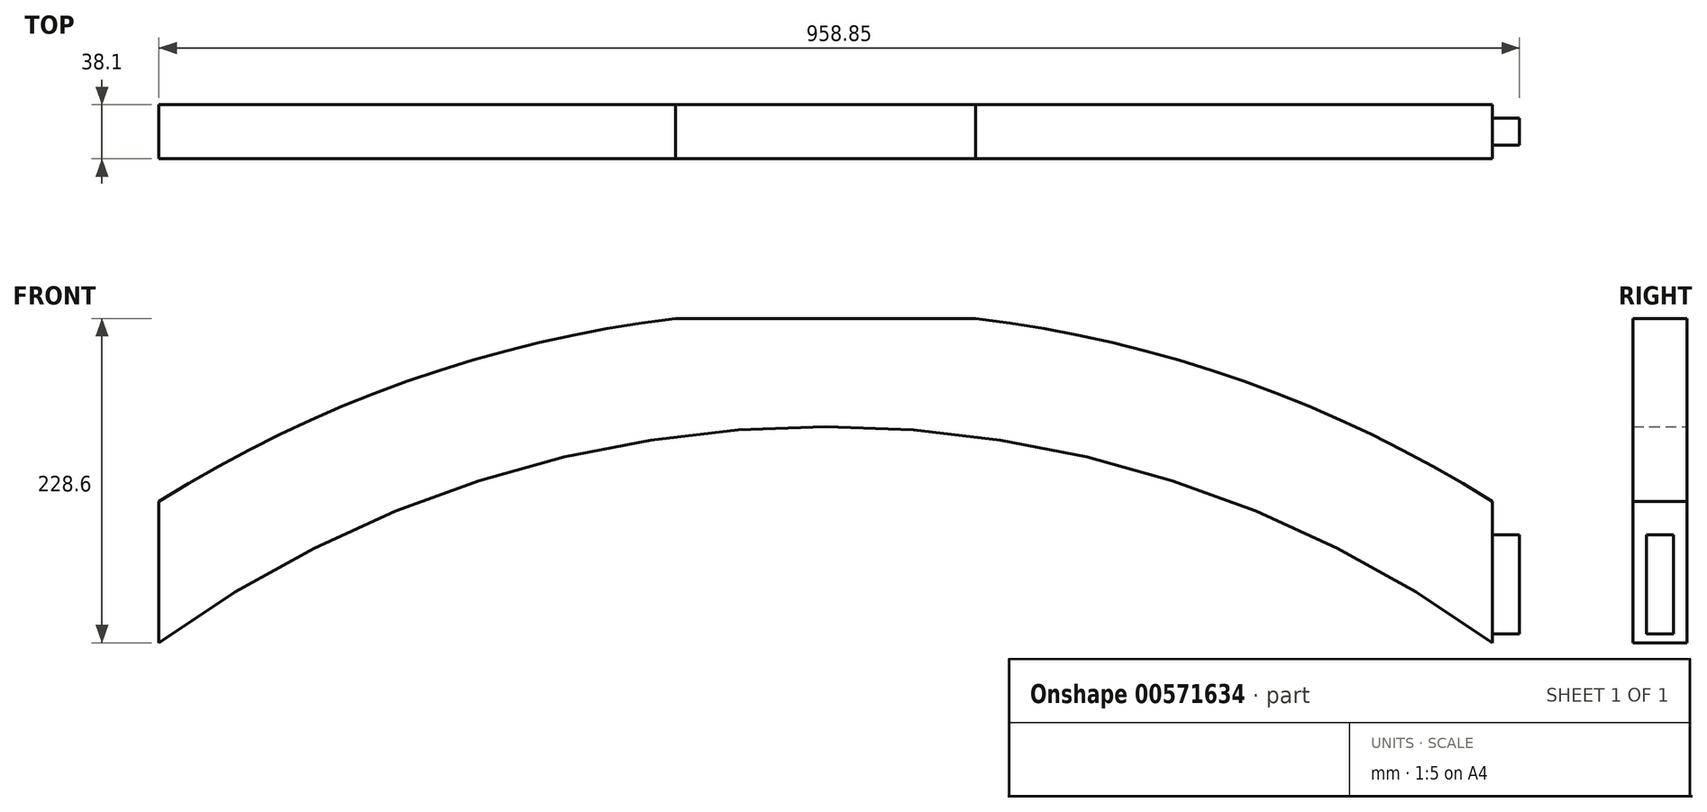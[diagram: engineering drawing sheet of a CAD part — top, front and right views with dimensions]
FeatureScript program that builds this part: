
annotation { "Feature Type Name" : "Feature", "Feature Type Description" : "" }
export const myFeature = defineFeature(function(context is Context, id is Id, definition is map)
    precondition{}
    {
        {
            var Q0;
            Q0=qCreatedBy(makeId("Front.planeOp"),FACE);
            var sketch = newSketch(context, id + "F0", { "sketchPlane" : qUnion([Q0])});
            skLineSegment(sketch, "E0.bottom", {"start": v(0, 0) * mm, "end": v(990.6, 0) * mm, "construction": true});
            skLineSegment(sketch, "E0.top", {"start": v(0, 375.92) * mm, "end": v(990.6, 375.92) * mm, "construction": true});
            skLineSegment(sketch, "E0.left", {"start": v(0, 0) * mm, "end": v(0, 375.92) * mm, "construction": true});
            skLineSegment(sketch, "E0.right", {"start": v(990.6, 0) * mm, "end": v(990.6, 375.92) * mm, "construction": true});
            skLineSegment(sketch, "E1", {"start": v(25.4, 366.92) * mm, "end": v(25.4, 21.35) * mm, "construction": true});
            skLineSegment(sketch, "E2", {"start": v(965.2, 14.82) * mm, "end": v(965.2, 359.55) * mm, "construction": true});
            skPoint(sketch, "E3", {"position": v(25.4, 147.32) * mm});
            skPoint(sketch, "E4", {"position": v(965.2, 147.32) * mm});
            skPoint(sketch, "E5", {"position": v(495.3, 299.72) * mm});
            skPoint(sketch, "E5.positionSnap0", {"position": v(495.3, 375.92) * mm});
            skArc(sketch, "E6", {"start": v(965.2, 147.32) * mm, "mid": v(495.3, 299.72) * mm, "end": v(25.4, 147.32) * mm});
            skArc(sketch, "E7.0", {"start": v(965.2, 246.89) * mm, "mid": v(790.25, 331.56) * mm, "end": v(601.02, 375.92) * mm});
            skLineSegment(sketch, "E8", {"start": v(25.4, 147.32) * mm, "end": v(25.4, 246.89) * mm});
            skLineSegment(sketch, "E9", {"start": v(965.2, 147.32) * mm, "end": v(965.2, 246.89) * mm});
            skArc(sketch, "E10.trimOffspring", {"start": v(389.58, 375.92) * mm, "mid": v(200.35, 331.56) * mm, "end": v(25.4, 246.89) * mm});
            skLineSegment(sketch, "E11", {"start": v(389.58, 375.92) * mm, "end": v(389.58, 375.92) * mm});
            skLineSegment(sketch, "E12", {"start": v(389.58, 375.92) * mm, "end": v(601.02, 375.92) * mm});
            skLineSegment(sketch, "E13.left", {"start": v(25.4, 217.17) * mm, "end": v(25.4, 153.67) * mm});
            skSolve(sketch);
        }
        {
            var Q0;
            {var subQ3=sQuery(id+"F0.wireOp",EDGE,"E6");Q0=makeQuery(id+"F0.imprint","IMPRINT",FACE,{"disambiguationData":[TD([[makeQuery(id+"F0.imprint","IMPRINT",EDGE,{"derivedFrom":subQ3}),-1.0]])]});}
            extrude(context, id + "F1", {"entities" : qUnion([Q0]), "depth" : 38.1 * mm, "offsetDistance" : 25.4 * mm});
        }
        {
            var Q0;
            Q0=makeQuery(id+"F1.opExtrude","SWEPT_FACE",FACE,{"disambiguationData":[OSD([sQuery(id+"F0.wireOp",EDGE,"E9")])]});
            var sketch = newSketch(context, id + "F2", { "sketchPlane" : qUnion([Q0])});
            skLineSegment(sketch, "E14.bottom", {"start": v(-28.58, 153.67) * mm, "end": v(-9.53, 153.67) * mm});
            skLineSegment(sketch, "E14.top", {"start": v(-28.58, 223.52) * mm, "end": v(-9.53, 223.52) * mm});
            skLineSegment(sketch, "E14.left", {"start": v(-28.58, 153.67) * mm, "end": v(-28.58, 223.52) * mm});
            skLineSegment(sketch, "E14.right", {"start": v(-9.53, 153.67) * mm, "end": v(-9.53, 223.52) * mm});
            skPoint(sketch, "E15", {"position": v(-19.05, 153.67) * mm});
            skPoint(sketch, "E16", {"position": v(-19.05, 147.32) * mm});
            skSolve(sketch);
        }
        {
            var Q0;
            Q0=makeQuery(id+"F2.imprint","IMPRINT",FACE,{"disambiguationData":[TD([[makeQuery(id+"F2.imprint","IMPRINT",EDGE,{"derivedFrom":sQuery(id+"F2.wireOp",EDGE,"E14.bottom")}),1.0]])]});
            extrude(context, id + "F3", {"entities" : qUnion([Q0]), "operationType" : NewBodyOperationType.ADD, "depth" : 19.05 * mm, "offsetDistance" : 25.4 * mm});
        }
        {
            var Q0;
            Q0=makeQuery(id+"F1.opExtrude","SWEPT_FACE",FACE,{"disambiguationData":[OSD([sQuery(id+"F0.wireOp",EDGE,"E9")])]});
            var Q1;
            Q1=makeQuery(id+"F1.opExtrude","SWEPT_FACE",FACE,{"disambiguationData":[OSD([sQuery(id+"F0.wireOp",EDGE,"E8"),sQuery(id+"F0.wireOp",EDGE,"E13.left")])]});
            cPlane(context, id + "F4", {"entities" : qUnion([Q0, Q1]), "cplaneType" : CPlaneType.MID_PLANE, "offset" : 25.4 * mm, "width" : 152.4 * mm, "height" : 152.4 * mm});
        }
    });
